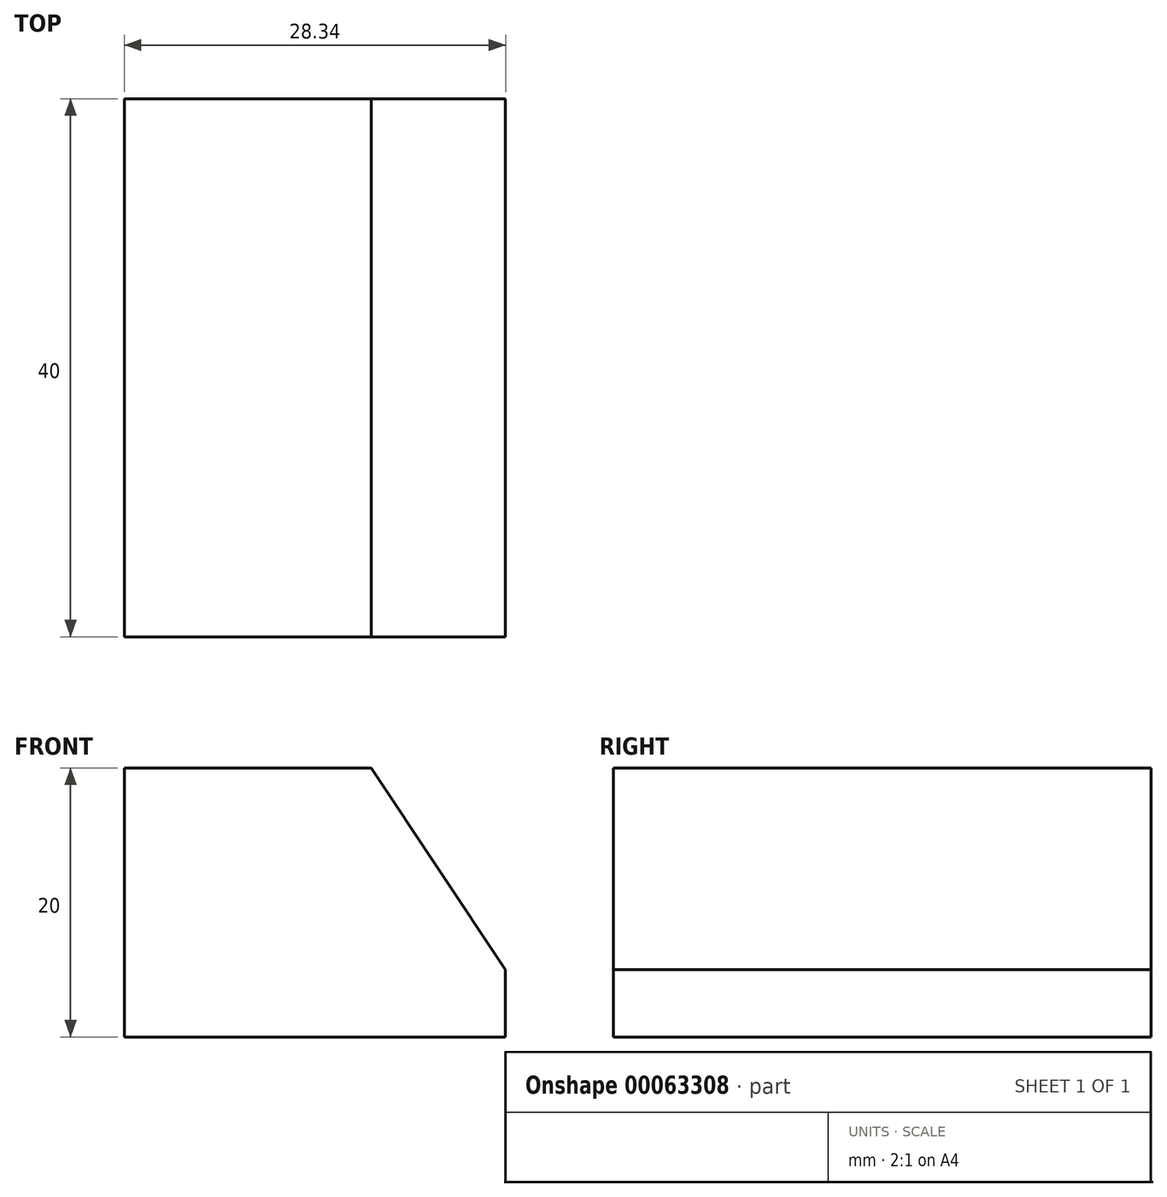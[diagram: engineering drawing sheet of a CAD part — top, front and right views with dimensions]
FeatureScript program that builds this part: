
annotation { "Feature Type Name" : "Feature", "Feature Type Description" : "" }
export const myFeature = defineFeature(function(context is Context, id is Id, definition is map)
    precondition{}
    {
        {
            var Q0;
            Q0=qCreatedBy(makeId("Top.planeOp"),FACE);
            var sketch = newSketch(context, id + "F0", { "sketchPlane" : qUnion([Q0])});
            skLineSegment(sketch, "E0.rect.bottom", {"start": v(21.5, -45) * mm, "end": v(-21.5, -45) * mm});
            skLineSegment(sketch, "E0.rect.top", {"start": v(21.5, 45) * mm, "end": v(-21.5, 45) * mm});
            skLineSegment(sketch, "E0.rect.left", {"start": v(21.5, -45) * mm, "end": v(21.5, 45) * mm});
            skLineSegment(sketch, "E0.rect.right", {"start": v(-21.5, -45) * mm, "end": v(-21.5, 45) * mm});
            skPoint(sketch, "E0.rect.middle", {"position": v(0, 0) * mm});
            skLineSegment(sketch, "E1", {"start": v(-21.5, -5) * mm, "end": v(21.5, -5) * mm});
            skLineSegment(sketch, "E2", {"start": v(-14.3, 45) * mm, "end": v(-14.3, -45) * mm});
            skLineSegment(sketch, "E3", {"start": v(14.04, 45) * mm, "end": v(14.04, -45) * mm});
            skSolve(sketch);
        }
        {
            var Q0;
            {var subQ0=sQuery(id+"F0.wireOp",EDGE,"E2");var subQ1=sQuery(id+"F0.wireOp",EDGE,"E0.rect.bottom");var subQ2=makeQuery(id+"F0.imprint","INTERSECT",VERTEX,{"derivedFrom":[subQ1,subQ0]});Q0=makeQuery(id+"F0.imprint","IMPRINT",FACE,{"disambiguationData":[TD([[makeQuery(id+"F0.imprint","IMPRINT",EDGE,{"disambiguationData":[TD([[subQ2,1.0]])],"derivedFrom":subQ1}),-1.0]])]});}
            extrude(context, id + "F1", {"entities" : qUnion([Q0]), "depth" : 20 * mm});
        }
        {
            var Q0;
            Q0=makeQuery(id+"F1.opExtrude","CAP_EDGE",EDGE,{"disambiguationData":[OSD([sQuery(id+"F0.wireOp",EDGE,"E3")])],"isStart":false});
            chamfer(context, id + "F2", {"entities" : qUnion([Q0]), "chamferType" : ChamferType.TWO_OFFSETS, "width1" : 15 * mm, "oppositeDirection" : false, "width2" : 10 * mm});
        }
    });
